# Revit family: FP_Revit_18_RS6121SRK1_Fridge_90001104A
name_source: partatom
category: Specialty Equipment
revit_build: Autodesk Revit 2018 (Build: 20170223_1515(x64)
units: mm (PartAtom-declared; Revit-internal decimal feet)

## family parameters
Always vertical = Yes
Cut with Voids When Loaded = Yes
OmniClass Number = 23.40.40.11.11
OmniClass Title = Refrigerators and Freezers
Part Type = Normal
Room Calculation Point = No
Round Connector Dimension = Use Diameter
Shared = No
Work Plane-Based = No

## types (2) — shared parameters
Cavity - Depth = 650 mm  [stored 2.13255 ft]
Cavity - Height = 2134 mm  [stored 7.00131 ft]
Cavity - Width = 610 mm  [stored 2.00131 ft]
Connector Description - Electrical = 230 V, 10 amp fused electrical supply
Handle Style - Contemporary Round (AHS-RD21) = No
Handle Style - Contemporary Square (AHD3-RD21) = No
Manufacturer = Fisher & Paykel Appliances
Material - Body = Fisher & Paykel - Grey
Material - Door Front = Fisher & Paykel - Stainless Steel
Material - Door Structure = Fisher & Paykel - White
Material - Handle = Fisher & Paykel - Aluminium
Product - Depth (exl front panel) = 610 mm  [stored 2.00131 ft]
Product - Height = 2134 mm  [stored 7.00131 ft]
Product - Width = 603 mm  [stored 1.97835 ft]
Stainless Steel Door Panels (RD6121R10D) = No
URL = www.fisherpaykel.com
Visibility - Clearance Required = Yes
Visibility - Visibility Control Note = Yes

## per-type parameters (varying)
| type | Connector Description - Water | Description | Visibility - Water Connection |
| RS6121SRK1 | Water Supply not required | 61cm Integrated Column Refrigerator, stainless steel interior | No |
| RS6121SRHK1 | 1/2 BSP Stainless steel braided hose | 61cm Integrated Column Refrigerator with internal water, stainless steel interior | Yes |

note: column(s) folded — value = type name in every type: Model

note: [stored X ft] marks values corroborated as IEEE doubles in the binary element streams (Revit-internal decimal feet)

## geometry (parser evidence)
native form markers: Sweep x8
no freeform markers — native parametric forms only
